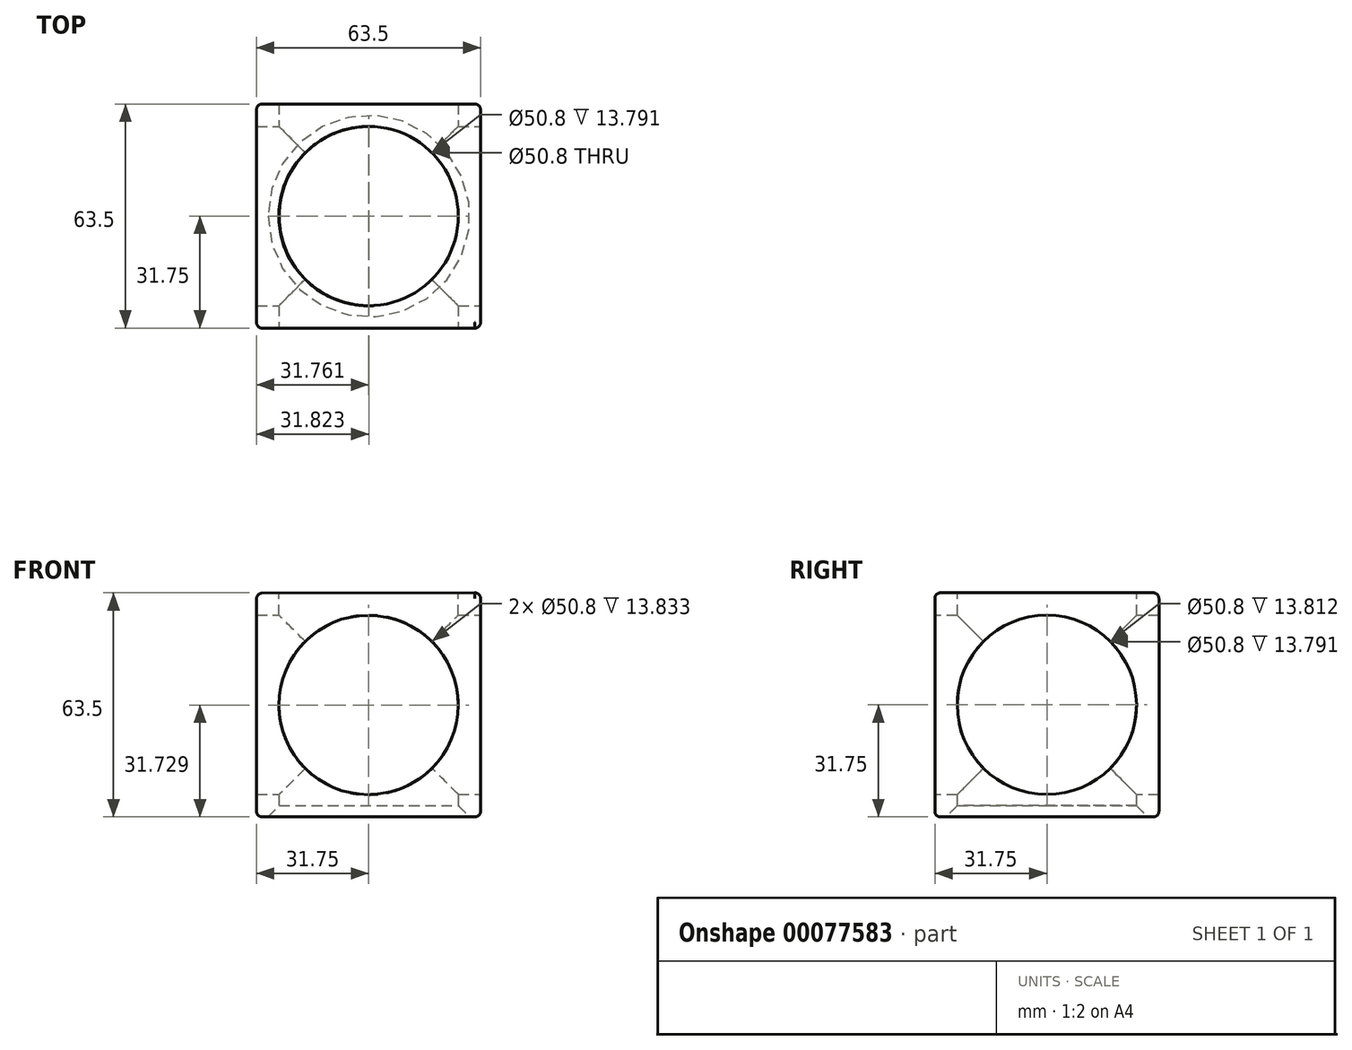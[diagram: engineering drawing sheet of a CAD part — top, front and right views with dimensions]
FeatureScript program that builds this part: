
annotation { "Feature Type Name" : "Feature", "Feature Type Description" : "" }
export const myFeature = defineFeature(function(context is Context, id is Id, definition is map)
    precondition{}
    {
        {
            var Q0;
            Q0=qCreatedBy(makeId("Front.planeOp"),FACE);
            var sketch = newSketch(context, id + "F0", { "sketchPlane" : qUnion([Q0])});
            skLineSegment(sketch, "E0", {"start": v(0, 0) * mm, "end": v(63.5, 0) * mm});
            skLineSegment(sketch, "E1", {"start": v(63.5, 0) * mm, "end": v(63.5, 63.5) * mm});
            skLineSegment(sketch, "E2", {"start": v(0, 63.42) * mm, "end": v(63.5, 63.5) * mm});
            skLineSegment(sketch, "E3", {"start": v(0, 63.42) * mm, "end": v(0, 0) * mm});
            skSolve(sketch);
        }
        {
            var Q0;
            Q0 = qSketchRegion(id + "F0", true);
            extrude(context, id + "F1", {"entities" : qUnion([Q0]), "depth" : 63.5 * mm});
        }
        {
            var Q0;
            Q0=makeQuery(id+"F1.opExtrude","CAP_FACE",FACE,{"disambiguationData":[OSD([sQuery(id+"F0.wireOp",EDGE,"E0"),sQuery(id+"F0.wireOp",EDGE,"E1"),sQuery(id+"F0.wireOp",EDGE,"E2"),sQuery(id+"F0.wireOp",EDGE,"E3")])],"isStart":false});
            var sketch = newSketch(context, id + "F2", { "sketchPlane" : qUnion([Q0])});
            skCircle(sketch, "E4", {"center": v(31.75, 31.73) * mm, "radius": 25.4 * mm});
            skSolve(sketch);
        }
        {
            var Q0;
            Q0 = qSketchRegion(id + "F2", true);
            extrude(context, id + "F3", {"entities" : qUnion([Q0]), "operationType" : NewBodyOperationType.REMOVE, "oppositeDirection" : true, "depth" : 63.5 * mm});
        }
        {
            var Q0;
            Q0=makeQuery(id+"F1.opExtrude","SWEPT_FACE",FACE,{"disambiguationData":[OSD([sQuery(id+"F0.wireOp",EDGE,"E1")])]});
            var sketch = newSketch(context, id + "F4", { "sketchPlane" : qUnion([Q0])});
            skCircle(sketch, "E5", {"center": v(-31.75, 31.75) * mm, "radius": 25.4 * mm});
            skSolve(sketch);
        }
        {
            var Q0;
            Q0 = qSketchRegion(id + "F4", true);
            extrude(context, id + "F5", {"entities" : qUnion([Q0]), "operationType" : NewBodyOperationType.REMOVE, "oppositeDirection" : true, "depth" : 63.5 * mm});
        }
        {
            var Q0;
            Q0=makeQuery(id+"F1.opExtrude","SWEPT_FACE",FACE,{"disambiguationData":[OSD([sQuery(id+"F0.wireOp",EDGE,"E2")])]});
            var sketch = newSketch(context, id + "F6", { "sketchPlane" : qUnion([Q0])});
            skCircle(sketch, "E6", {"center": v(31.83, -31.75) * mm, "radius": 25.4 * mm});
            skCircle(sketch, "E7", {"center": v(63.58, -31.75) * mm, "radius": 2.3 * mm});
            skSolve(sketch);
        }
        {
            var Q0;
            Q0=makeQuery(id+"F6.imprint","IMPRINT",FACE,{"disambiguationData":[TD([[makeQuery(id+"F6.imprint","IMPRINT",EDGE,{"derivedFrom":sQuery(id+"F6.wireOp",EDGE,"E6")}),1.0]])]});
            extrude(context, id + "F7", {"entities" : qUnion([Q0]), "operationType" : NewBodyOperationType.REMOVE, "oppositeDirection" : true, "depth" : 63.5 * mm});
        }
        {
            var Q0;
            Q0=makeQuery(id+"F5.boolean.opBoolean","COPY",EDGE,{"derivedFrom":makeQuery(id+"F5.opExtrude","CAP_EDGE",EDGE,{"disambiguationData":[OSD([sQuery(id+"F4.wireOp",EDGE,"E5")])],"isStart":true})});
            var Q1;
            Q1=makeQuery(id+"F3.boolean.opBoolean","COPY",EDGE,{"derivedFrom":makeQuery(id+"F3.opExtrude","CAP_EDGE",EDGE,{"disambiguationData":[OSD([sQuery(id+"F2.wireOp",EDGE,"E4")])],"isStart":true})});
            var Q2;
            Q2=makeQuery(id+"F3.boolean.opBoolean","COPY",EDGE,{"derivedFrom":makeQuery(id+"F3.opExtrude","CAP_EDGE",EDGE,{"disambiguationData":[OSD([sQuery(id+"F2.wireOp",EDGE,"E4")])],"isStart":false})});
            var Q3;
            Q3=makeQuery(id+"F5.boolean.opBoolean","COPY",EDGE,{"derivedFrom":makeQuery(id+"F5.opExtrude","CAP_EDGE",EDGE,{"disambiguationData":[OSD([sQuery(id+"F4.wireOp",EDGE,"E5")])],"isStart":false})});
            var Q4;
            Q4=makeQuery(id+"F7.boolean.opBoolean","COPY",EDGE,{"derivedFrom":makeQuery(id+"F7.opExtrude","CAP_EDGE",EDGE,{"disambiguationData":[OSD([sQuery(id+"F6.wireOp",EDGE,"E6")])],"isStart":true})});
            var Q5;
            Q5=makeQuery(id+"F7.boolean.opBoolean","INTERSECT",EDGE,{"derivedFrom":[makeQuery(id+"F1.opExtrude","SWEPT_FACE",FACE,{"disambiguationData":[OSD([sQuery(id+"F0.wireOp",EDGE,"E0")])]}),makeQuery(id+"F7.opExtrude","SWEPT_FACE",FACE,{"disambiguationData":[OSD([sQuery(id+"F6.wireOp",EDGE,"E6")])]})]});
            chamfer(context, id + "F8", {"entities" : qUnion([Q0, Q1, Q2, Q3, Q4, Q5]), "width" : 3.17 * mm, "tangentPropagation" : true});
        }
        {
            var Q0;
            Q0=makeQuery(id+"F1.opExtrude","SWEPT_EDGE",EDGE,{"disambiguationData":[OSD([sQuery(id+"F0.wireOp",EDGE,"E1"),sQuery(id+"F0.wireOp",EDGE,"E2")])]});
            var Q1;
            Q1=makeQuery(id+"F1.opExtrude","CAP_EDGE",EDGE,{"disambiguationData":[OSD([sQuery(id+"F0.wireOp",EDGE,"E2")])],"isStart":false});
            var Q2;
            Q2=makeQuery(id+"F1.opExtrude","CAP_EDGE",EDGE,{"disambiguationData":[OSD([sQuery(id+"F0.wireOp",EDGE,"E2")])],"isStart":true});
            var Q3;
            Q3=makeQuery(id+"F1.opExtrude","SWEPT_EDGE",EDGE,{"disambiguationData":[OSD([sQuery(id+"F0.wireOp",EDGE,"E2"),sQuery(id+"F0.wireOp",EDGE,"E3")])]});
            var Q4;
            Q4=makeQuery(id+"F1.opExtrude","CAP_EDGE",EDGE,{"disambiguationData":[OSD([sQuery(id+"F0.wireOp",EDGE,"E3")])],"isStart":true});
            var Q5;
            Q5=makeQuery(id+"F1.opExtrude","CAP_EDGE",EDGE,{"disambiguationData":[OSD([sQuery(id+"F0.wireOp",EDGE,"E0")])],"isStart":true});
            var Q6;
            Q6=makeQuery(id+"F1.opExtrude","CAP_EDGE",EDGE,{"disambiguationData":[OSD([sQuery(id+"F0.wireOp",EDGE,"E1")])],"isStart":true});
            var Q7;
            Q7=makeQuery(id+"F1.opExtrude","CAP_EDGE",EDGE,{"disambiguationData":[OSD([sQuery(id+"F0.wireOp",EDGE,"E3")])],"isStart":false});
            var Q8;
            Q8=makeQuery(id+"F1.opExtrude","SWEPT_EDGE",EDGE,{"disambiguationData":[OSD([sQuery(id+"F0.wireOp",EDGE,"E0"),sQuery(id+"F0.wireOp",EDGE,"E3")])]});
            var Q9;
            Q9=makeQuery(id+"F1.opExtrude","SWEPT_EDGE",EDGE,{"disambiguationData":[OSD([sQuery(id+"F0.wireOp",EDGE,"E0"),sQuery(id+"F0.wireOp",EDGE,"E1")])]});
            var Q10;
            Q10=makeQuery(id+"F1.opExtrude","CAP_EDGE",EDGE,{"disambiguationData":[OSD([sQuery(id+"F0.wireOp",EDGE,"E0")])],"isStart":false});
            fillet(context, id + "F9", {"entities" : qUnion([Q0, Q1, Q2, Q3, Q4, Q5, Q6, Q7, Q8, Q9, Q10]), "radius" : 1.59 * mm, "tangentPropagation" : true, "allowEdgeOverflow" : false});
        }
        {
            var Q0;
            Q0=makeQuery(id+"F1.opExtrude","CAP_EDGE",EDGE,{"disambiguationData":[OSD([sQuery(id+"F0.wireOp",EDGE,"E1")])],"isStart":false});
            var Q1;
            {var subQ0=sQuery(id+"F0.wireOp",EDGE,"E1");Q1=makeQuery(id+"F9.opFillet","BLEND_EDGE",EDGE,{"blendedFrom":[makeQuery(id+"F1.opExtrude","SWEPT_EDGE",EDGE,{"disambiguationData":[OSD([sQuery(id+"F0.wireOp",EDGE,"E0"),subQ0])]}),makeQuery(id+"F1.opExtrude","SWEPT_FACE",FACE,{"disambiguationData":[OSD([subQ0])]})],"blendedInto":[makeQuery(id+"F1.opExtrude","SWEPT_FACE",FACE,{"disambiguationData":[OSD([subQ0])]})]});}
            fillet(context, id + "F10", {"entities" : qUnion([Q0, Q1]), "radius" : 1.59 * mm, "tangentPropagation" : true, "allowEdgeOverflow" : false});
        }
    });
